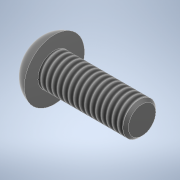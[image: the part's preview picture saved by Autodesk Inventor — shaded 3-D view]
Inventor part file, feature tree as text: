
AUTODESK INVENTOR PART (.ipt)
format: ipt  version: 2022 (Build 260153000, 153)  size: 139,776 bytes
history: native  units: mm
features: sketch x2, revolve x1, extrude x1, thread x1, chamfer x1
ambient origin geometry x8: Origin, YZ Plane, XZ Plane, XY Plane, X Axis, Y Axis, Z Axis, Center Point
bodies: Solid1 (feature_tree)
feature tree (6):
  revolve  "Revolution1"  [1 undecoded]
  extrude  "Extrusion1"  Depth=2.0mm
  thread  "Thread1"  [1 undecoded]
  chamfer  "Chamfer1"  Distance=2.0mm
  sketch  "Sketch1"  dims[d0=1.5mm d1=3.0mm]
  sketch  "Sketch2"  dims[d2=5.5mm d3=3.0mm d4=8.0mm d5=2.0mm d6=90.0deg d7=2.0mm d8=1.0mm d9=0.0mm d10=6.0mm d11=0.0mm d12=0.25mm d13=2.0mm d14=45.0deg]
note: 2 required parameter values undecoded (feature->parameter linkage not recoverable at this tier; creation-order binding heuristic only, values carry confidence <= 0.55)